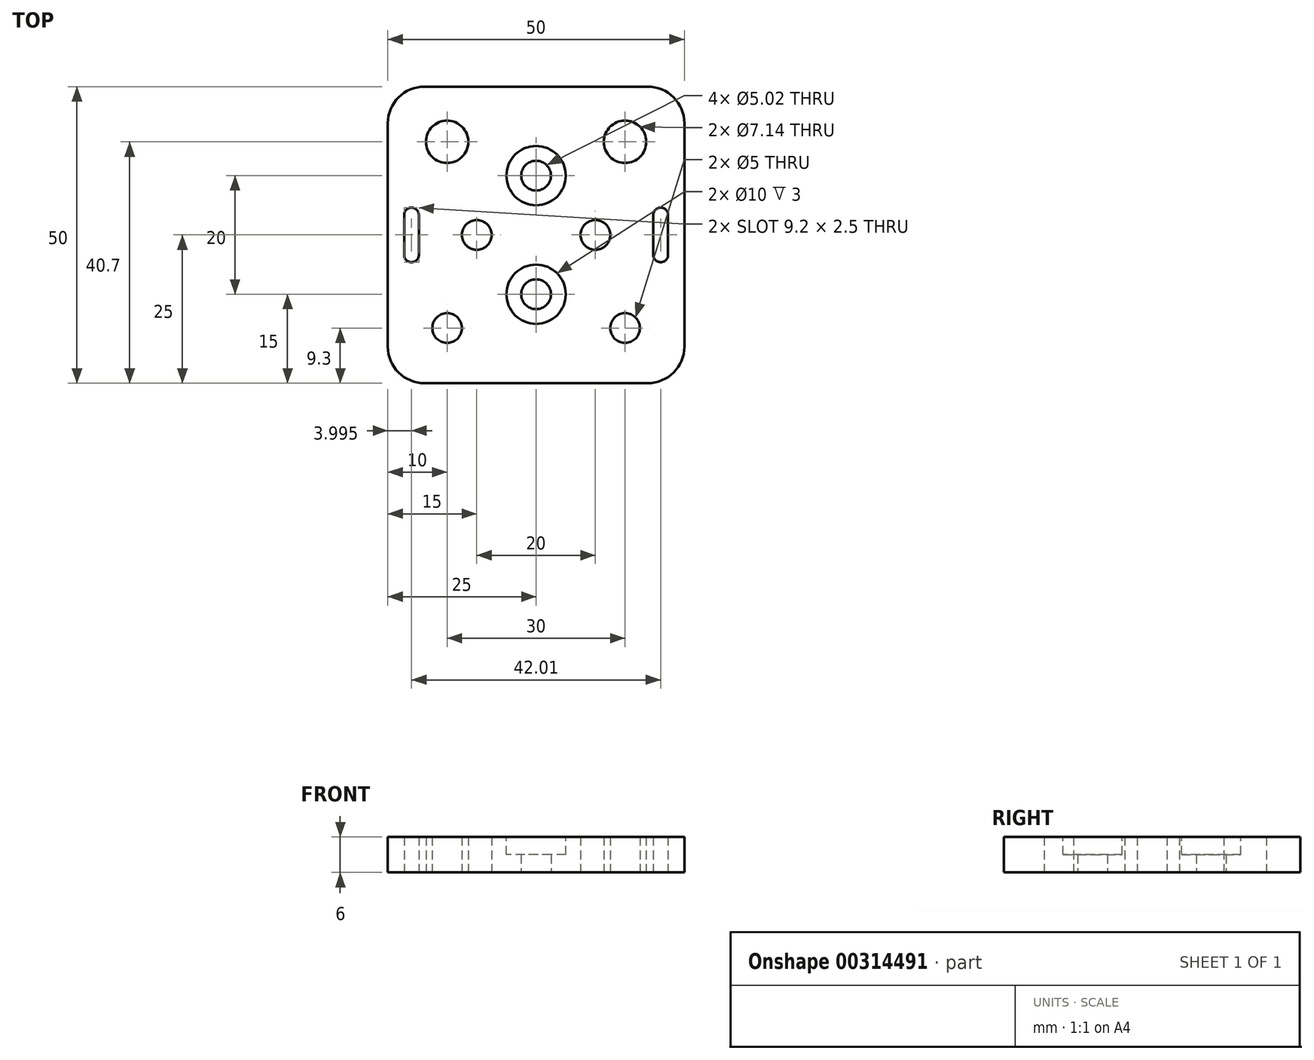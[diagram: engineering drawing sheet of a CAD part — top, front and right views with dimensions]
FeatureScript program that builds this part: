
annotation { "Feature Type Name" : "Feature", "Feature Type Description" : "" }
export const myFeature = defineFeature(function(context is Context, id is Id, definition is map)
    precondition{}
    {
        {
            var Q0;
            Q0=qCreatedBy(makeId("Top.planeOp"),FACE);
            var sketch = newSketch(context, id + "F0", { "sketchPlane" : qUnion([Q0])});
            skCircle(sketch, "E0", {"center": v(-15, 15.7) * mm, "radius": 3.57 * mm});
            skCircle(sketch, "E1", {"center": v(15, 15.7) * mm, "radius": 3.57 * mm});
            skCircle(sketch, "E2", {"center": v(-15, -15.7) * mm, "radius": 2.5 * mm});
            skCircle(sketch, "E3", {"center": v(15, -15.7) * mm, "radius": 2.5 * mm});
            skLineSegment(sketch, "E4", {"start": v(-22.25, 3.35) * mm, "end": v(-22.25, -3.35) * mm});
            skLineSegment(sketch, "E5", {"start": v(-19.75, 3.35) * mm, "end": v(-19.75, -3.35) * mm});
            skLineSegment(sketch, "E6", {"start": v(19.75, 3.35) * mm, "end": v(19.75, -3.35) * mm});
            skLineSegment(sketch, "E7", {"start": v(22.25, 3.35) * mm, "end": v(22.25, -3.35) * mm});
            skCircle(sketch, "E8", {"center": v(0, 10) * mm, "radius": 2.5 * mm});
            skCircle(sketch, "E9", {"center": v(-10, 0) * mm, "radius": 2.5 * mm});
            skCircle(sketch, "E10", {"center": v(0, -10) * mm, "radius": 2.5 * mm});
            skCircle(sketch, "E11", {"center": v(10, 0) * mm, "radius": 2.5 * mm});
            skArc(sketch, "E12", {"start": v(-18.83, 25) * mm, "mid": v(-23.2, 23.2) * mm, "end": v(-25, 18.83) * mm});
            skLineSegment(sketch, "E13", {"start": v(18.83, 25) * mm, "end": v(-18.83, 25) * mm});
            skArc(sketch, "E14", {"start": v(25, 18.83) * mm, "mid": v(23.2, 23.2) * mm, "end": v(18.83, 25) * mm});
            skLineSegment(sketch, "E15", {"start": v(25, -18.83) * mm, "end": v(25, 18.83) * mm});
            skArc(sketch, "E16", {"start": v(18.83, -25) * mm, "mid": v(23.2, -23.2) * mm, "end": v(25, -18.83) * mm});
            skLineSegment(sketch, "E17", {"start": v(-25, -18.83) * mm, "end": v(-25, 18.83) * mm});
            skLineSegment(sketch, "E18", {"start": v(-18.83, -25) * mm, "end": v(18.83, -25) * mm});
            skArc(sketch, "E19", {"start": v(-25, -18.83) * mm, "mid": v(-23.2, -23.2) * mm, "end": v(-18.83, -25) * mm});
            skArc(sketch, "E20", {"start": v(-22.25, -3.35) * mm, "mid": v(-21, -4.6) * mm, "end": v(-19.75, -3.35) * mm});
            skArc(sketch, "E21", {"start": v(-19.75, 3.35) * mm, "mid": v(-21, 4.6) * mm, "end": v(-22.26, 3.35) * mm});
            skArc(sketch, "E22", {"start": v(19.75, -3.35) * mm, "mid": v(21, -4.6) * mm, "end": v(22.25, -3.35) * mm});
            skArc(sketch, "E23", {"start": v(22.25, 3.35) * mm, "mid": v(21, 4.6) * mm, "end": v(19.75, 3.35) * mm});
            skSolve(sketch);
        }
        {
            var Q0;
            Q0 = qSketchRegion(id + "F0", true);
            extrude(context, id + "F1", {"entities" : qUnion([Q0]), "depth" : 6 * mm});
        }
        {
            var Q0;
            Q0=makeQuery(id+"F1.opExtrude","CAP_FACE",FACE,{"disambiguationData":[OSD([sQuery(id+"F0.wireOp",EDGE,"E0"),sQuery(id+"F0.wireOp",EDGE,"E1"),sQuery(id+"F0.wireOp",EDGE,"E2"),sQuery(id+"F0.wireOp",EDGE,"E3"),sQuery(id+"F0.wireOp",EDGE,"d5e0a3e2-3234-4d1f-9e68-26090fdee558"),sQuery(id+"F0.wireOp",EDGE,"44c231e4-4a07-417f-a716-a3f30e5c64d7"),sQuery(id+"F0.wireOp",EDGE,"c7973675-0f27-4e93-8ab5-1c968797fa5f"),sQuery(id+"F0.wireOp",EDGE,"85be8226-b8f7-4a96-88a5-9965953cbbf0"),sQuery(id+"F0.wireOp",EDGE,"E4"),sQuery(id+"F0.wireOp",EDGE,"E5"),sQuery(id+"F0.wireOp",EDGE,"E6"),sQuery(id+"F0.wireOp",EDGE,"E7"),sQuery(id+"F0.wireOp",EDGE,"E8"),sQuery(id+"F0.wireOp",EDGE,"E9"),sQuery(id+"F0.wireOp",EDGE,"E10"),sQuery(id+"F0.wireOp",EDGE,"E11"),sQuery(id+"F0.wireOp",EDGE,"E12"),sQuery(id+"F0.wireOp",EDGE,"E13"),sQuery(id+"F0.wireOp",EDGE,"E14"),sQuery(id+"F0.wireOp",EDGE,"E15"),sQuery(id+"F0.wireOp",EDGE,"E16"),sQuery(id+"F0.wireOp",EDGE,"E17"),sQuery(id+"F0.wireOp",EDGE,"E18"),sQuery(id+"F0.wireOp",EDGE,"E19")])],"isStart":false});
            var sketch = newSketch(context, id + "F2", { "sketchPlane" : qUnion([Q0])});
            skCircle(sketch, "E24", {"center": v(0, 10) * mm, "radius": 5 * mm});
            skCircle(sketch, "E25", {"center": v(0, -10) * mm, "radius": 5 * mm});
            skSolve(sketch);
        }
        {
            var Q0;
            Q0 = qSketchRegion(id + "F2", true);
            extrude(context, id + "F3", {"entities" : qUnion([Q0]), "operationType" : NewBodyOperationType.REMOVE, "oppositeDirection" : true, "depth" : 3 * mm});
        }
    });
